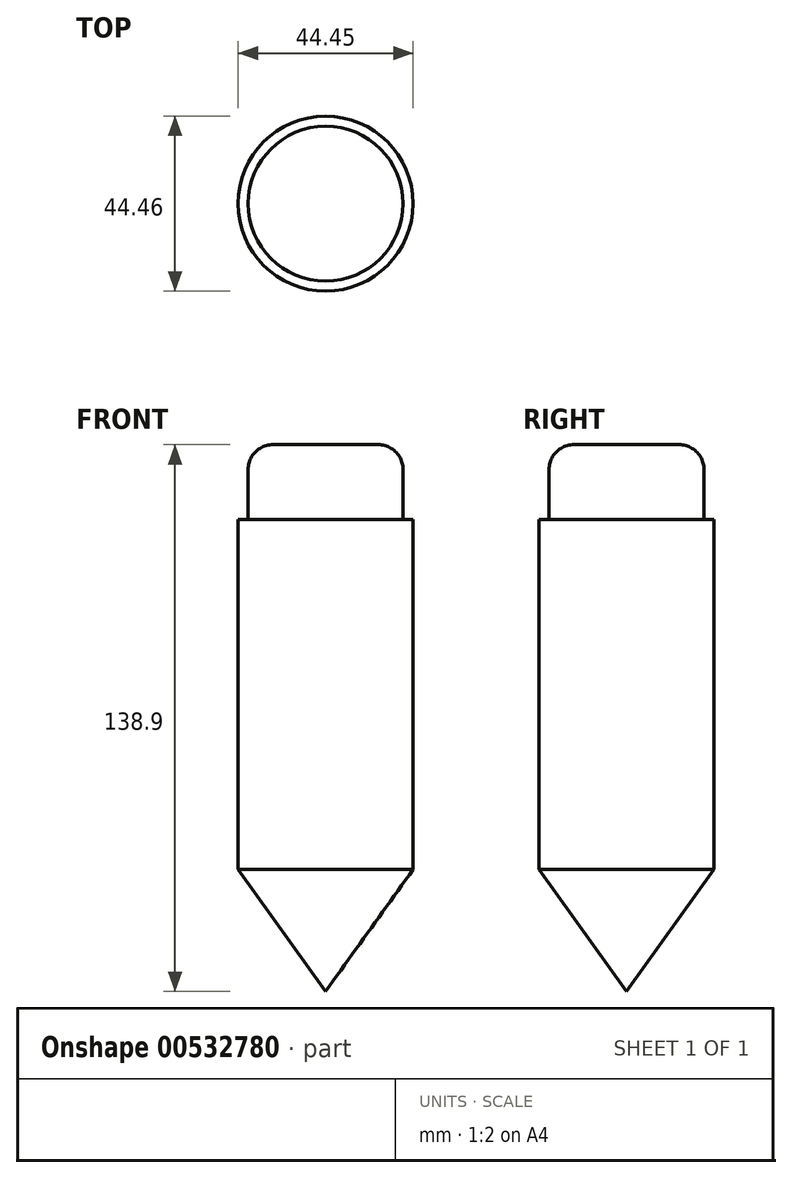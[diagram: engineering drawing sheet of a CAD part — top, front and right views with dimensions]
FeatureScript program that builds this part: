
annotation { "Feature Type Name" : "Feature", "Feature Type Description" : "" }
export const myFeature = defineFeature(function(context is Context, id is Id, definition is map)
    precondition{}
    {
        {
            var Q0;
            Q0=qCreatedBy(makeId("Front.planeOp"),FACE);
            var sketch = newSketch(context, id + "F0", { "sketchPlane" : qUnion([Q0])});
            skLineSegment(sketch, "E0.top", {"start": v(3.19, -55.62) * mm, "end": v(47.64, -55.62) * mm});
            skLineSegment(sketch, "E0.left", {"start": v(3.19, 33.28) * mm, "end": v(3.19, -55.62) * mm});
            skLineSegment(sketch, "E0.right", {"start": v(47.64, 33.28) * mm, "end": v(47.64, -55.62) * mm});
            skLineSegment(sketch, "E1", {"start": v(3.19, 33.28) * mm, "end": v(47.64, 33.28) * mm});
            skLineSegment(sketch, "E2.bottom", {"start": v(5.73, 33.28) * mm, "end": v(45.1, 33.28) * mm});
            skLineSegment(sketch, "E2.top", {"start": v(5.73, 52.33) * mm, "end": v(45.1, 52.33) * mm});
            skLineSegment(sketch, "E2.left", {"start": v(5.73, 33.28) * mm, "end": v(5.73, 52.33) * mm});
            skLineSegment(sketch, "E2.right", {"start": v(45.1, 33.28) * mm, "end": v(45.1, 52.33) * mm});
            skLineSegment(sketch, "E3", {"start": v(25.41, -86.57) * mm, "end": v(25.41, 88.83) * mm});
            skPoint(sketch, "E3.endSnap0", {"position": v(25.41, 52.33) * mm});
            skLineSegment(sketch, "E4", {"start": v(3.19, -55.62) * mm, "end": v(25.41, -86.57) * mm});
            skLineSegment(sketch, "E5", {"start": v(47.64, -55.62) * mm, "end": v(25.41, -86.57) * mm});
            skSolve(sketch);
        }
        {
            var Q0;
            {var subQ5=sQuery(id+"F0.wireOp",EDGE,"E0.left");Q0=makeQuery(id+"F0.imprint","IMPRINT",FACE,{"disambiguationData":[TD([[makeQuery(id+"F0.imprint","IMPRINT",EDGE,{"derivedFrom":subQ5}),1.0]])]});}
            var Q1;
            {var subQ0=sQuery(id+"F0.wireOp",EDGE,"E2.left");Q1=makeQuery(id+"F0.imprint","IMPRINT",FACE,{"disambiguationData":[TD([[makeQuery(id+"F0.imprint","IMPRINT",EDGE,{"derivedFrom":subQ0}),-1.0]])]});}
            var Q2;
            {var subQ0=sQuery(id+"F0.wireOp",EDGE,"E4");Q2=makeQuery(id+"F0.imprint","IMPRINT",FACE,{"disambiguationData":[TD([[makeQuery(id+"F0.imprint","IMPRINT",EDGE,{"derivedFrom":subQ0}),1.0]])]});}
            var Q3;
            Q3=sQuery(id+"F0.wireOp",EDGE,"E3");
            revolve(context, id + "F1", {"entities" : qUnion([Q0, Q1, Q2]), "axis" : qUnion([Q3]), "revolveType" : RevolveType.FULL});
        }
        {
            var Q0;
            Q0=makeQuery(id+"F1.opRevolve","SWEPT_EDGE",EDGE,{"disambiguationData":[OSD([sQuery(id+"F0.wireOp",EDGE,"E2.top"),sQuery(id+"F0.wireOp",EDGE,"E2.left")])]});
            fillet(context, id + "F2", {"entities" : qUnion([Q0]), "radius" : 6.35 * mm, "tangentPropagation" : true, "allowEdgeOverflow" : false});
        }
    });
